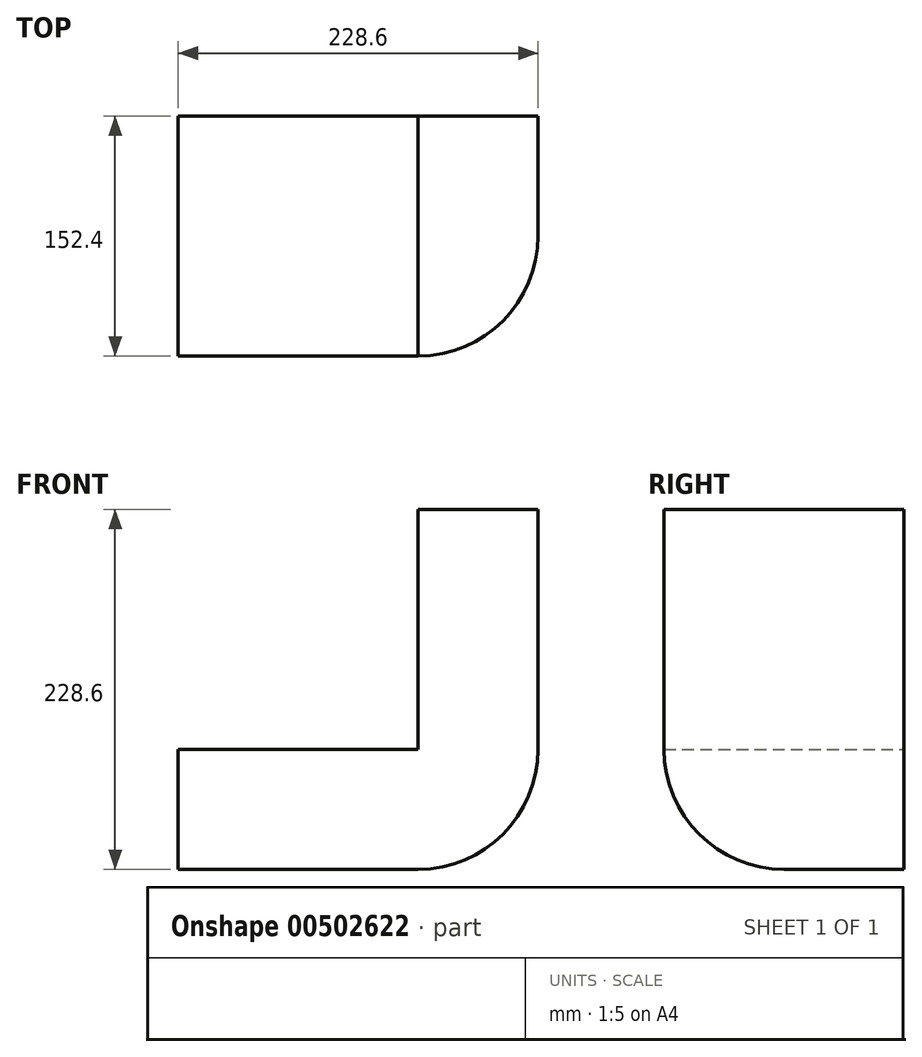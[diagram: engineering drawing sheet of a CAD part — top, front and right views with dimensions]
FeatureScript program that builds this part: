
annotation { "Feature Type Name" : "Feature", "Feature Type Description" : "" }
export const myFeature = defineFeature(function(context is Context, id is Id, definition is map)
    precondition{}
    {
        {
            var Q0;
            Q0=qCreatedBy(makeId("Front.planeOp"),FACE);
            var sketch = newSketch(context, id + "F0", { "sketchPlane" : qUnion([Q0])});
            skLineSegment(sketch, "E0.bottom", {"start": v(-118.08, 51.5) * mm, "end": v(110.52, 51.5) * mm});
            skLineSegment(sketch, "E0.top", {"start": v(-118.08, -24.7) * mm, "end": v(110.52, -24.7) * mm});
            skLineSegment(sketch, "E0.left", {"start": v(-118.08, 51.5) * mm, "end": v(-118.08, -24.7) * mm});
            skLineSegment(sketch, "E0.right", {"start": v(110.52, 51.5) * mm, "end": v(110.52, -24.7) * mm});
            skSolve(sketch);
        }
        {
            var Q0;
            Q0=makeQuery(id+"F0.imprint","IMPRINT",FACE,{"disambiguationData":[TD([[makeQuery(id+"F0.imprint","IMPRINT",EDGE,{"derivedFrom":sQuery(id+"F0.wireOp",EDGE,"E0.bottom")}),-1.0]])]});
            extrude(context, id + "F1", {"entities" : qUnion([Q0]), "depth" : 152.4 * mm});
        }
        {
            var Q0;
            Q0=makeQuery(id+"F1.opExtrude","SWEPT_FACE",FACE,{"disambiguationData":[OSD([sQuery(id+"F0.wireOp",EDGE,"E0.right")])]});
            var sketch = newSketch(context, id + "F2", { "sketchPlane" : qUnion([Q0])});
            skLineSegment(sketch, "E1.bottom", {"start": v(-152.4, -24.7) * mm, "end": v(0, -24.7) * mm});
            skLineSegment(sketch, "E1.top", {"start": v(-152.4, 203.9) * mm, "end": v(0, 203.9) * mm});
            skLineSegment(sketch, "E1.left", {"start": v(-152.4, -24.7) * mm, "end": v(-152.4, 203.9) * mm});
            skLineSegment(sketch, "E1.right", {"start": v(0, -24.7) * mm, "end": v(0, 203.9) * mm});
            skSolve(sketch);
        }
        {
            var Q0;
            {var subQ0=sQuery(id+"F2.wireOp",EDGE,"E1.top");Q0=makeQuery(id+"F2.imprint","IMPRINT",FACE,{"disambiguationData":[TD([[makeQuery(id+"F2.imprint","IMPRINT",EDGE,{"derivedFrom":subQ0}),-1.0]])]});}
            var Q1;
            {var subQ0=sQuery(id+"F2.wireOp",EDGE,"E1.bottom");Q1=makeQuery(id+"F2.imprint","IMPRINT",FACE,{"disambiguationData":[TD([[makeQuery(id+"F2.imprint","IMPRINT",EDGE,{"derivedFrom":subQ0}),1.0]])]});}
            extrude(context, id + "F3", {"entities" : qUnion([Q0, Q1]), "operationType" : NewBodyOperationType.ADD, "oppositeDirection" : true, "depth" : 76.2 * mm});
        }
        {
            var Q0;
            Q0=makeQuery(id+"F1.opExtrude","CAP_EDGE",EDGE,{"disambiguationData":[OSD([sQuery(id+"F0.wireOp",EDGE,"E0.top")])],"isStart":false});
            fillet(context, id + "F4", {"entities" : qUnion([Q0]), "radius" : 76.2 * mm, "tangentPropagation" : true, "allowEdgeOverflow" : false});
        }
        {
            var Q0;
            Q0=makeQuery(id+"F3.boolean.opBoolean","MERGE",EDGE,{"derivedFrom":[makeQuery(id+"F1.opExtrude","CAP_EDGE",EDGE,{"disambiguationData":[OSD([sQuery(id+"F0.wireOp",EDGE,"E0.right")])],"isStart":false}),makeQuery(id+"F3.opExtrude","CAP_EDGE",EDGE,{"disambiguationData":[OSD([sQuery(id+"F2.wireOp",EDGE,"E1.left")])],"isStart":true})]});
            fillet(context, id + "F5", {"entities" : qUnion([Q0]), "radius" : 76.2 * mm, "tangentPropagation" : true, "allowEdgeOverflow" : false});
        }
    });
